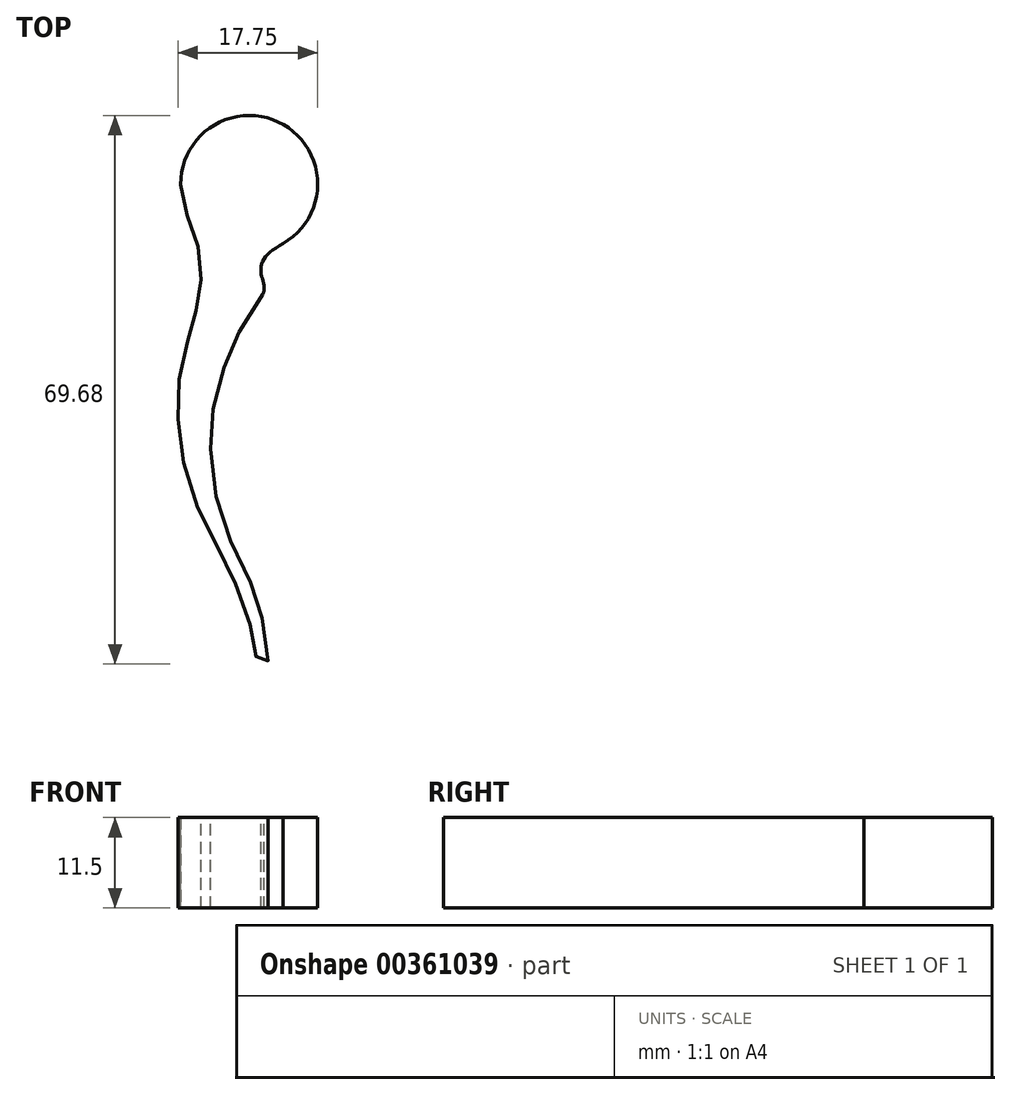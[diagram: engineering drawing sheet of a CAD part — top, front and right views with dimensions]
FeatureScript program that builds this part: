
annotation { "Feature Type Name" : "Feature", "Feature Type Description" : "" }
export const myFeature = defineFeature(function(context is Context, id is Id, definition is map)
    precondition{}
    {
        {
            var Q0;
            Q0=qCreatedBy(makeId("Front.planeOp"),FACE);
            var sketch = newSketch(context, id + "F0", { "sketchPlane" : qUnion([Q0])});
            skLineSegment(sketch, "E0", {"start": v(0, 13.47) * mm, "end": v(0, -2.36) * mm});
            skLineSegment(sketch, "E1", {"start": v(-3.06, 0) * mm, "end": v(-23.5, 0) * mm});
            skSolve(sketch);
        }
        {
            var Q0;
            Q0=qCreatedBy(makeId("Top.planeOp"),FACE);
            var sketch = newSketch(context, id + "F1", { "sketchPlane" : qUnion([Q0])});
            skCircle(sketch, "E2", {"center": v(-2.51, -18.35) * mm, "radius": 8.7 * mm});
            skFitSpline(sketch, "E3", {"points": [v(-9.91, -22.93) * mm, v(-11, -21.2) * mm, v(-11.87, -20.34) * mm, v(-12.7, -19.94) * mm, v(-13.45, -19.83) * mm, v(-14.18, -19.9) * mm, v(-14.87, -20.12) * mm, v(-15.48, -20.22) * mm, v(-16.2, -20.18) * mm, v(-16.86, -19.83) * mm], "startDerivative": vector(-6.58, 11.1) * mm, "endDerivative": vector(-9.99, 6.24) * mm});
            skFitSpline(sketch, "E4", {"points": [v(-16.86, -19.83) * mm, v(-19.31, -18.27) * mm, v(-20.97, -17.25) * mm, v(-23.22, -16.1) * mm, v(-24.77, -15.5) * mm, v(-27.47, -14.62) * mm, v(-30.13, -13.95) * mm, v(-32.07, -13.62) * mm, v(-34.64, -13.43) * mm, v(-36.96, -13.46) * mm, v(-40.57, -13.8) * mm, v(-43.39, -14.44) * mm, v(-45.8, -15.15) * mm, v(-50.23, -17.13) * mm, v(-52.32, -18.17) * mm, v(-54.13, -18.96) * mm, v(-56.07, -19.6) * mm, v(-58.14, -20.1) * mm, v(-61.41, -20.57) * mm, v(-63.2, -20.75) * mm, v(-63.4, -20.67) * mm, v(-63.5, -20.29) * mm, v(-63.42, -19.83) * mm, v(-63.12, -19.46) * mm, v(-62.36, -19.13) * mm, v(-60.32, -18.72) * mm, v(-59.21, -18.6) * mm, v(-57.78, -18.3) * mm, v(-55.27, -17.46) * mm, v(-52.3, -16.17) * mm, v(-49.75, -14.88) * mm, v(-47.43, -13.67) * mm, v(-45.17, -12.48) * mm, v(-43.18, -11.62) * mm, v(-40.41, -10.62) * mm, v(-36.82, -9.8) * mm, v(-34.27, -9.46) * mm, v(-31.7, -9.3) * mm, v(-29.18, -9.35) * mm, v(-27.2, -9.49) * mm, v(-25.3, -9.82) * mm, v(-22.93, -10.43) * mm, v(-21.17, -10.93) * mm, v(-19.87, -11.3) * mm, v(-18.45, -11.64) * mm, v(-16.86, -11.94) * mm, v(-15.29, -12.17) * mm, v(-14.45, -12.22) * mm, v(-12.94, -12.21) * mm, v(-11.4, -12) * mm, v(-9.1, -11.49) * mm, v(-7.59, -10.89) * mm, v(-6.55, -10.5) * mm, v(-5.64, -10.13) * mm, v(-4.5, -9.81) * mm, v(-2.59, -9.65) * mm], "startDerivative": vector(-117.97, 74.9) * mm, "endDerivative": vector(125.91, -0.19) * mm});
            skSolve(sketch);
        }
        {
            var Q0;
            Q0 = qSketchRegion(id + "F1", true);
            extrude(context, id + "F2", {"entities" : qUnion([Q0]), "depth" : 11.5 * mm});
        }
        {
            var Q0;
            Q0=makeQuery(id+"F2.opExtrude","SWEPT_BODY",BODY,{"disambiguationData":[OSD([sQuery(id+"F1.wireOp",EDGE,"E2"),sQuery(id+"F1.wireOp",EDGE,"E3"),sQuery(id+"F1.wireOp",EDGE,"E4")])]});
            var Q1;
            Q1=sQuery(id+"F0.wireOp",EDGE,"E0");
            transform(context, id + "F3", {"entities" : qUnion([Q0]), "transformType" : TransformType.ROTATION, "transformAxis" : qUnion([Q1]), "angle" : 90 * degree, "oppositeDirection" : true, "makeCopy" : false});
        }
        {
            var Q0;
            Q0=makeQuery(id+"F2.opExtrude","SWEPT_BODY",BODY,{"disambiguationData":[OSD([sQuery(id+"F1.wireOp",EDGE,"E2"),sQuery(id+"F1.wireOp",EDGE,"E3"),sQuery(id+"F1.wireOp",EDGE,"E4")])]});
            var Q1;
            Q1=makeQuery(id+"F2.opExtrude","CAP_VERTEX",VERTEX,{"disambiguationData":[OSD([sQuery(id+"F1.wireOp",EDGE,"E2"),sQuery(id+"F1.wireOp",EDGE,"E4")])],"isStart":false});
            var Q2;
            Q2=qCreatedBy(makeId("Origin.pointOp"),VERTEX);
            transform(context, id + "F4", {"entities" : qUnion([Q0]), "transformType" : TransformType.TRANSLATION_ENTITY, "oppositeDirectionEntity" : false, "transformLine" : qUnion([Q1, Q2]), "makeCopy" : false});
        }
        {
            var Q0;
            Q0=makeQuery(id+"F2.opExtrude","SWEPT_BODY",BODY,{"disambiguationData":[OSD([sQuery(id+"F1.wireOp",EDGE,"E2"),sQuery(id+"F1.wireOp",EDGE,"E3"),sQuery(id+"F1.wireOp",EDGE,"E4")])]});
            var Q1;
            Q1=makeQuery(id+"F2.opExtrude","CAP_EDGE",EDGE,{"disambiguationData":[OSD([sQuery(id+"F1.wireOp",EDGE,"E2")])],"isStart":false});
            var Q2;
            Q2=qCreatedBy(makeId("Origin.pointOp"),VERTEX);
            transform(context, id + "F5", {"entities" : qUnion([Q0]), "transformType" : TransformType.TRANSLATION_ENTITY, "oppositeDirectionEntity" : false, "transformLine" : qUnion([Q1, Q2]), "makeCopy" : false});
        }
        {
            var Q0;
            Q0=makeQuery(id+"F2.opExtrude","SWEPT_BODY",BODY,{"disambiguationData":[OSD([sQuery(id+"F1.wireOp",EDGE,"E2"),sQuery(id+"F1.wireOp",EDGE,"E3"),sQuery(id+"F1.wireOp",EDGE,"E4")])]});
            var Q1;
            Q1=qCreatedBy(makeId("Front.planeOp"),FACE);
            transform(context, id + "F6", {"entities" : qUnion([Q0]), "transformType" : TransformType.TRANSLATION_DISTANCE, "transformDirection" : qUnion([Q1]), "distance" : 20 * mm, "makeCopy" : false});
        }
        {
            var Q0;
            Q0=makeQuery(id+"F2.opExtrude","SWEPT_BODY",BODY,{"disambiguationData":[OSD([sQuery(id+"F1.wireOp",EDGE,"E2"),sQuery(id+"F1.wireOp",EDGE,"E3"),sQuery(id+"F1.wireOp",EDGE,"E4")])]});
            var Q1;
            Q1=qCreatedBy(makeId("Right.planeOp"),FACE);
            transform(context, id + "F7", {"entities" : qUnion([Q0]), "transformType" : TransformType.TRANSLATION_DISTANCE, "transformDirection" : qUnion([Q1]), "distance" : 15 * mm, "oppositeDirection" : true, "makeCopy" : false});
        }
    });
